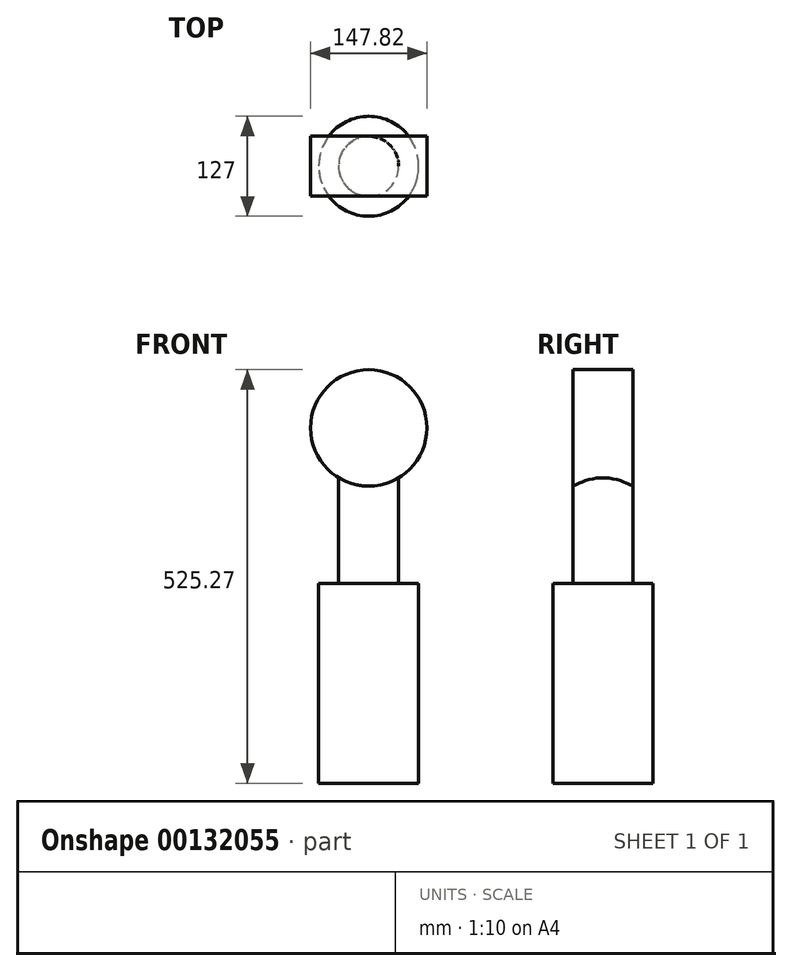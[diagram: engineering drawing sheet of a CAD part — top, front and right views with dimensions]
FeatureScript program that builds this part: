
annotation { "Feature Type Name" : "Feature", "Feature Type Description" : "" }
export const myFeature = defineFeature(function(context is Context, id is Id, definition is map)
    precondition{}
    {
        {
            var Q0;
            Q0=qCreatedBy(makeId("Top.planeOp"),FACE);
            var sketch = newSketch(context, id + "F0", { "sketchPlane" : qUnion([Q0])});
            skCircle(sketch, "E0", {"center": v(0, 0) * mm, "radius": 63.5 * mm});
            skSolve(sketch);
        }
        {
            var Q0;
            Q0=makeQuery(id+"F0.imprint","IMPRINT",FACE,{"disambiguationData":[TD([[makeQuery(id+"F0.imprint","IMPRINT",EDGE,{"derivedFrom":sQuery(id+"F0.wireOp",EDGE,"E0")}),1.0]])]});
            extrude(context, id + "F1", {"entities" : qUnion([Q0]), "depth" : 254 * mm});
        }
        {
            var Q0;
            Q0=makeQuery(id+"F1.opExtrude","CAP_FACE",FACE,{"disambiguationData":[OSD([sQuery(id+"F0.wireOp",EDGE,"E0")])],"isStart":false});
            var sketch = newSketch(context, id + "F3", { "sketchPlane" : qUnion([Q0])});
            skCircle(sketch, "E1", {"center": v(0, 0) * mm, "radius": 38.1 * mm});
            skSolve(sketch);
        }
        {
            var Q0;
            Q0 = qSketchRegion(id + "F3", true);
            extrude(context, id + "F2", {"entities" : qUnion([Q0]), "operationType" : NewBodyOperationType.ADD, "depth" : 152.4 * mm});
        }
        {
            var Q0;
            Q0=qCreatedBy(makeId("Right.planeOp"),FACE);
            var sketch = newSketch(context, id + "F4", { "sketchPlane" : qUnion([Q0])});
            skLineSegment(sketch, "E2.bottom", {"start": v(38.1, 451.37) * mm, "end": v(-38.1, 451.37) * mm});
            skLineSegment(sketch, "E2.top", {"start": v(38.1, 377.46) * mm, "end": v(-38.1, 377.46) * mm});
            skLineSegment(sketch, "E2.left", {"start": v(38.1, 451.37) * mm, "end": v(38.1, 377.46) * mm});
            skLineSegment(sketch, "E2.right", {"start": v(-38.1, 451.37) * mm, "end": v(-38.1, 377.46) * mm});
            skPoint(sketch, "E2.middle", {"position": v(0, 414.41) * mm});
            skSolve(sketch);
        }
        {
            var Q0;
            Q0=makeQuery(id+"F4.imprint","IMPRINT",FACE,{"disambiguationData":[TD([[makeQuery(id+"F4.imprint","IMPRINT",EDGE,{"derivedFrom":sQuery(id+"F4.wireOp",EDGE,"E2.bottom")}),1.0]])]});
            var Q1;
            Q1=sQuery(id+"F4.wireOp",EDGE,"E2.bottom");
            revolve(context, id + "F5", {"operationType" : NewBodyOperationType.ADD, "entities" : qUnion([Q0]), "axis" : qUnion([Q1]), "revolveType" : RevolveType.FULL});
        }
    });
